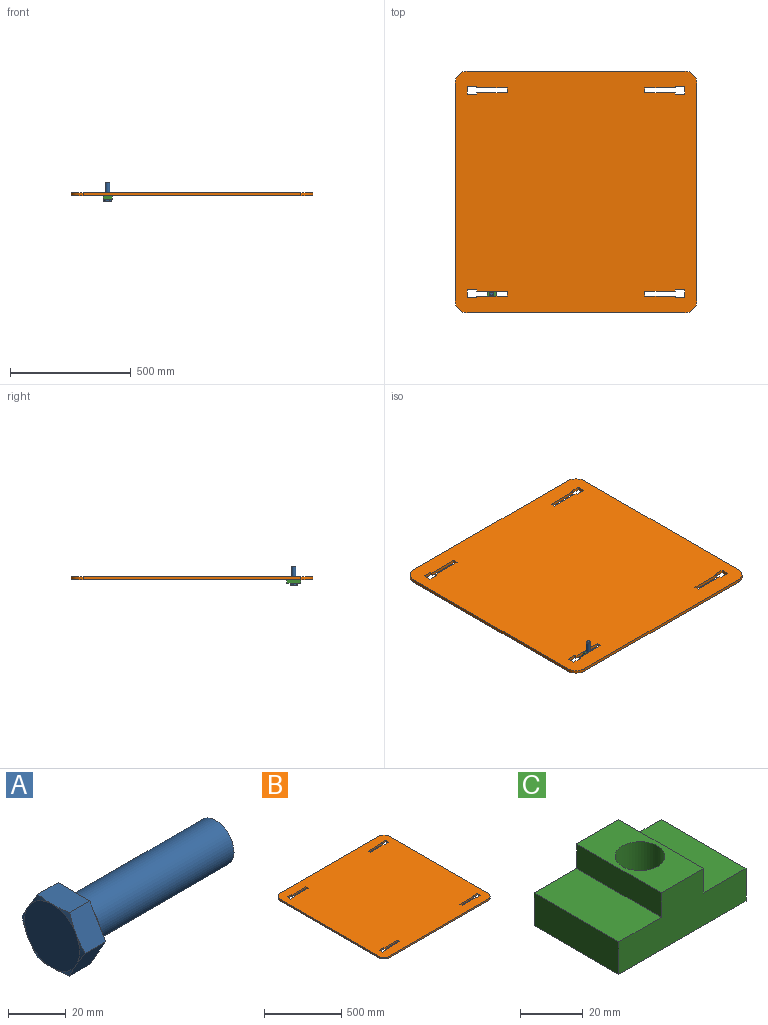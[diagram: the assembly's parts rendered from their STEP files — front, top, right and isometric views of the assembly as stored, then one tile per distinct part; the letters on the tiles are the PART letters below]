
ASSEMBLY  parts=3 mates=3
PART A: 20 faces, bbox 82.7x32.4x32.4 mm
  f0: plane 27x27mm, normal (-1,0,0), area 572.6mm2, adj f1,f2,f3,f4,f5,f6
  f1: cone r=15.6mm half-angle=70deg, axis (1,0,0), area 16.5mm2, adj f0,f7,f8
  f2: cone r=15.6mm half-angle=70deg, axis (1,0,0), area 16.5mm2, adj f0,f8,f9
  f3: cone r=15.6mm half-angle=70deg, axis (1,0,0), area 16.5mm2, adj f0,f9,f10
  f4: cone r=15.6mm half-angle=70deg, axis (1,0,0), area 16.5mm2, adj f0,f10,f11
  f5: cone r=15.6mm half-angle=70deg, axis (1,0,0), area 16.5mm2, adj f0,f7,f12
  f6: cone r=15.6mm half-angle=70deg, axis (1,0,0), area 16.5mm2, adj f0,f11,f12
  f7: plane 14.69x11.89mm, normal (0,0.87,-0.5), area 162.7mm2, adj f1,f5,f8,f12,f13
  f8: plane 14.69x11.89mm, normal (0,0.87,0.5), area 162.7mm2, adj f1,f2,f7,f9,f13
  f9: plane 16.78x11.89mm, normal (0,0,1), area 162.7mm2, adj f2,f3,f8,f10,f13
  f10: plane 14.69x11.89mm, normal (0,-0.87,0.5), area 162.7mm2, adj f3,f4,f9,f11,f13
  f11: plane 14.69x11.89mm, normal (0,-0.87,-0.5), area 162.7mm2, adj f4,f6,f10,f12,f13
  f12: plane 16.78x11.89mm, normal (0,0,-1), area 162.7mm2, adj f5,f6,f7,f11,f13
  f13: plane 31.18x27mm, normal (1,0,0), area 127mm2, adj f7,f8,f9,f10,f11,f12,f14
  f14: cylinder r=12.67mm len=25.34mm, axis (-1,0,0), area 63.7mm2, adj f13,f15
  f15: plane 25.34x25.34mm, normal (1,0,0), area 215.7mm2, adj f14,f17
  f16: plane 14.93x14.93mm, normal (1,0,0), area 175.1mm2, adj f18
  f17: torus R=9.6mm, axis (-1,0,0), area 54.6mm2, adj f15,f19
  f18: cone r=9mm half-angle=55deg, axis (-1,0,0), area 96.8mm2, adj f16,f19
  f19: cylinder r=9mm len=68.33mm, axis (-1,0,0), area 3863.8mm2, adj f17,f18
PART B: 42 faces, bbox 1000x1000x12.7 mm
  f0: plane 38.1x12.7mm, normal (0,-1,0), area 483.9mm2, adj f1,f39,f40,f41
  f1: plane 12.7x6.48mm, normal (-1,0,0), area 82.3mm2, adj f0,f2,f40,f41
  f2: plane 127x12.7mm, normal (0,-1,0), area 1612.9mm2, adj f1,f3,f40,f41
  f3: plane 19.05x12.7mm, normal (-1,0,0), area 241.9mm2, adj f2,f4,f40,f41
  f4: plane 127x12.7mm, normal (0,1,0), area 1612.9mm2, adj f3,f5,f40,f41
  f5: plane 12.7x6.48mm, normal (-1,0,0), area 82.3mm2, adj f4,f6,f40,f41
  f6: plane 38.1x12.7mm, normal (0,1,0), area 483.9mm2, adj f5,f39,f40,f41
  f7: plane 12.7x6.48mm, normal (1,0,0), area 82.3mm2, adj f8,f35,f40,f41
  f8: plane 38.1x12.7mm, normal (0,-1,0), area 483.9mm2, adj f7,f9,f40,f41
  f9: plane 32x12.7mm, normal (-1,0,0), area 406.5mm2, adj f8,f10,f40,f41
  f10: plane 38.1x12.7mm, normal (0,1,0), area 483.9mm2, adj f9,f11,f40,f41
  f11: plane 12.7x6.48mm, normal (1,0,0), area 82.3mm2, adj f10,f12,f40,f41
  f12: plane 127x12.7mm, normal (0,1,0), area 1612.9mm2, adj f11,f13,f40,f41
  f13: plane 19.05x12.7mm, normal (1,0,0), area 241.9mm2, adj f12,f35,f40,f41
  f14: plane 12.7x6.48mm, normal (1,0,0), area 82.3mm2, adj f15,f36,f40,f41
  f15: plane 38.1x12.7mm, normal (0,-1,0), area 483.9mm2, adj f14,f16,f40,f41
  f16: plane 32x12.7mm, normal (-1,0,0), area 406.5mm2, adj f15,f17,f40,f41
  f17: plane 38.1x12.7mm, normal (0,1,0), area 483.9mm2, adj f16,f18,f40,f41
  f18: plane 12.7x6.48mm, normal (1,0,0), area 82.3mm2, adj f17,f19,f40,f41
  f19: plane 127x12.7mm, normal (0,1,0), area 1612.9mm2, adj f18,f20,f40,f41
  f20: plane 19.05x12.7mm, normal (1,0,0), area 241.9mm2, adj f19,f36,f40,f41
  f21: plane 38.1x12.7mm, normal (0,1,0), area 483.9mm2, adj f22,f37,f40,f41
  f22: plane 32x12.7mm, normal (1,0,0), area 406.5mm2, adj f21,f23,f40,f41
  f23: plane 38.1x12.7mm, normal (0,-1,0), area 483.9mm2, adj f22,f24,f40,f41
  f24: plane 12.7x6.48mm, normal (-1,0,0), area 82.3mm2, adj f23,f25,f40,f41
  f25: plane 127x12.7mm, normal (0,-1,0), area 1612.9mm2, adj f24,f26,f40,f41
  f26: plane 19.05x12.7mm, normal (-1,0,0), area 241.9mm2, adj f25,f27,f40,f41
  f27: plane 127x12.7mm, normal (0,1,0), area 1612.9mm2, adj f26,f37,f40,f41
  f28: plane 898.4x12.7mm, normal (0,1,0), area 11409.7mm2, adj f29,f38,f40,f41
  f29: cylinder r=50.8mm len=50.8mm, axis (0,0,-1), area 1013.4mm2, adj f28,f30,f40,f41
  f30: plane 898.4x12.7mm, normal (-1,0,0), area 11409.7mm2, adj f29,f31,f40,f41
  f31: cylinder r=50.8mm len=50.8mm, axis (0,0,-1), area 1013.4mm2, adj f30,f32,f40,f41
  f32: plane 898.4x12.7mm, normal (0,-1,0), area 11409.7mm2, adj f31,f33,f40,f41
  f33: cylinder r=50.8mm len=50.8mm, axis (0,0,-1), area 1013.4mm2, adj f32,f34,f40,f41
  f34: plane 898.4x12.7mm, normal (1,0,0), area 11409.7mm2, adj f33,f38,f40,f41
  f35: plane 127x12.7mm, normal (0,-1,0), area 1612.9mm2, adj f7,f13,f40,f41
  f36: plane 127x12.7mm, normal (0,-1,0), area 1612.9mm2, adj f14,f20,f40,f41
  f37: plane 12.7x6.48mm, normal (-1,0,0), area 82.3mm2, adj f21,f27,f40,f41
  f38: cylinder r=50.8mm len=50.8mm, axis (0,0,-1), area 1013.4mm2, adj f28,f34,f40,f41
  f39: plane 32x12.7mm, normal (1,0,0), area 406.5mm2, adj f0,f6,f40,f41
  f40: plane 1000x1000mm, normal (0,0,1), area 983230mm2, adj f0,f1,f2,f3,f4,f5,f6,f7
  f41: plane 1000x1000mm, normal (0,0,-1), area 983230mm2, adj f0,f1,f2,f3,f4,f5,f6,f7
PART C: 11 faces, bbox 57.2x38.1x22.2 mm
  f0: plane 38.1x18.92mm, normal (0,0,1), area 523mm2, adj f1,f7,f8,f9,f10
  f1: plane 38.1x9.53mm, normal (-1,0,0), area 362.9mm2, adj f0,f2,f8,f9
  f2: plane 38.1x19.11mm, normal (0,0,1), area 728.2mm2, adj f1,f3,f8,f9
  f3: plane 38.1x12.7mm, normal (-1,0,0), area 483.9mm2, adj f2,f4,f8,f9
  f4: plane 57.15x38.1mm, normal (0,0,-1), area 1979.5mm2, adj f3,f5,f8,f9,f10
  f5: plane 38.1x12.7mm, normal (1,0,0), area 483.9mm2, adj f4,f6,f8,f9
  f6: plane 38.1x19.11mm, normal (0,0,1), area 728.2mm2, adj f5,f7,f8,f9
  f7: plane 38.1x9.53mm, normal (1,0,0), area 362.9mm2, adj f0,f6,f8,f9
  f8: plane 57.15x22.23mm, normal (0,-1,0), area 906mm2, adj f0,f1,f2,f3,f4,f5,f6,f7
  f9: plane 57.15x22.23mm, normal (0,1,0), area 906mm2, adj f0,f1,f2,f3,f4,f5,f6,f7
  f10: cylinder r=7.94mm len=22.23mm, axis (0,0,1), area 1108.4mm2, adj f0,f4
PLACE A rot(axis=(0.19,-0.96,0.19),92.2deg) t=(-380.13,-347.63,607.38)mm
PLACE B t=(-31.58,72.81,620.26)mm
PLACE C rot(axis=(0,0,-1),90deg) t=(-361.08,-347.63,614.6)mm
MATE planar C.f2 <-> B.f41  axis (0,0,1) through (-380.13,-328.61,620.26)mm
MATE planar C.f1 <-> B.f2  axis (0,1,0) through (-380.13,-338.16,625.02)mm
MATE revolute C.f10 <-> A.f1  axis (0,0,-1) through (-380.13,-347.63,607.56)mm
